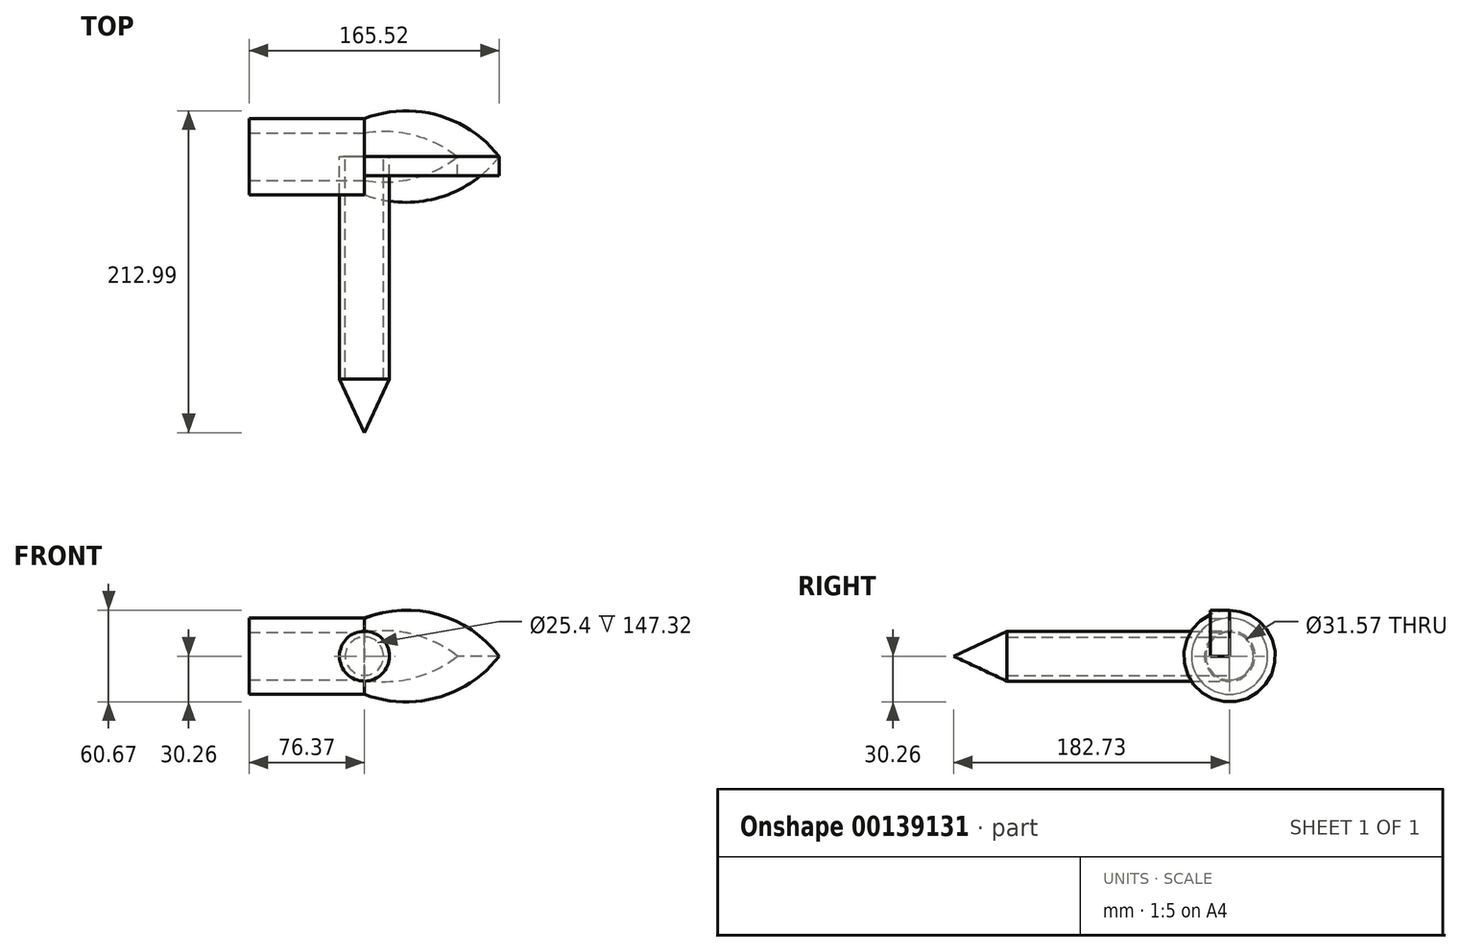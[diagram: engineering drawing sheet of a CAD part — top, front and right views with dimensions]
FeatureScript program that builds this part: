
annotation { "Feature Type Name" : "Feature", "Feature Type Description" : "" }
export const myFeature = defineFeature(function(context is Context, id is Id, definition is map)
    precondition{}
    {
        {
            var Q0;
            Q0=qCreatedBy(makeId("Front.planeOp"),FACE);
            var sketch = newSketch(context, id + "F0", { "sketchPlane" : qUnion([Q0])});
            skCircle(sketch, "E0", {"center": v(0, 0) * mm, "radius": 12.7 * mm});
            skCircle(sketch, "E1", {"center": v(0, 0) * mm, "radius": 16.51 * mm});
            skSolve(sketch);
        }
        {
            var Q0;
            Q0 = qSketchRegion(id + "F0", true);
            extrude(context, id + "F1", {"entities" : qUnion([Q0]), "depth" : 147.32 * mm});
        }
        {
            var Q0;
            Q0=makeQuery(id+"F1.opExtrude","CAP_FACE",FACE,{"disambiguationData":[OSD([sQuery(id+"F0.wireOp",EDGE,"E0"),sQuery(id+"F0.wireOp",EDGE,"E1")])],"isStart":false});
            var sketch = newSketch(context, id + "F2", { "sketchPlane" : qUnion([Q0])});
            skCircle(sketch, "E2.0", {"center": v(0, 0) * mm, "radius": 16.51 * mm});
            skSolve(sketch);
        }
        {
            var Q0;
            Q0 = qSketchRegion(id + "F2", true);
            extrude(context, id + "F3", {"entities" : qUnion([Q0]), "operationType" : NewBodyOperationType.ADD, "depth" : 38.1 * mm, "hasDraft" : true, "draftAngle" : 25 * degree, "draftPullDirection" : true});
        }
        {
            var Q0;
            Q0=qCreatedBy(makeId("Front.planeOp"),FACE);
            var sketch = newSketch(context, id + "F4", { "sketchPlane" : qUnion([Q0])});
            skArc(sketch, "E3", {"start": v(89.15, 0) * mm, "mid": v(48.73, 27.31) * mm, "end": v(0, 25.23) * mm});
            skLineSegment(sketch, "E4", {"start": v(89.15, 0) * mm, "end": v(61.53, 0) * mm});
            skArc(sketch, "E5", {"start": v(61.53, 0) * mm, "mid": v(32.43, 14.4) * mm, "end": v(0, 15.79) * mm});
            skLineSegment(sketch, "E6", {"start": v(0, 25.23) * mm, "end": v(-76.37, 25.23) * mm});
            skLineSegment(sketch, "E7.bottom", {"start": v(0, 15.79) * mm, "end": v(-76.37, 15.79) * mm});
            skLineSegment(sketch, "E7.right", {"start": v(-76.37, 15.79) * mm, "end": v(-76.37, 25.23) * mm});
            skSolve(sketch);
        }
        {
            var Q0;
            Q0 = qSketchRegion(id + "F4", true);
            var Q1;
            Q1=sQuery(id+"F4.wireOp",EDGE,"E4");
            revolve(context, id + "F5", {"entities" : qUnion([Q0]), "axis" : qUnion([Q1]), "revolveType" : RevolveType.FULL});
        }
        {
            var Q0;
            Q0=qCreatedBy(makeId("Front.planeOp"),FACE);
            var sketch = newSketch(context, id + "F6", { "sketchPlane" : qUnion([Q0])});
            skLineSegment(sketch, "E8", {"start": v(0, 25.05) * mm, "end": v(0, 15.87) * mm});
            skLineSegment(sketch, "E9", {"start": v(89.05, 0) * mm, "end": v(61.51, 0) * mm});
            skArc(sketch, "E10", {"start": v(89.05, 0) * mm, "mid": v(48.76, 27.56) * mm, "end": v(0, 25.05) * mm});
            skArc(sketch, "E11", {"start": v(61.51, 0) * mm, "mid": v(32.4, 14.32) * mm, "end": v(0, 15.87) * mm});
            skSolve(sketch);
        }
        {
            var Q0;
            Q0 = qSketchRegion(id + "F6", true);
            extrude(context, id + "F7", {"entities" : qUnion([Q0]), "depth" : 12.7 * mm});
        }
    });
